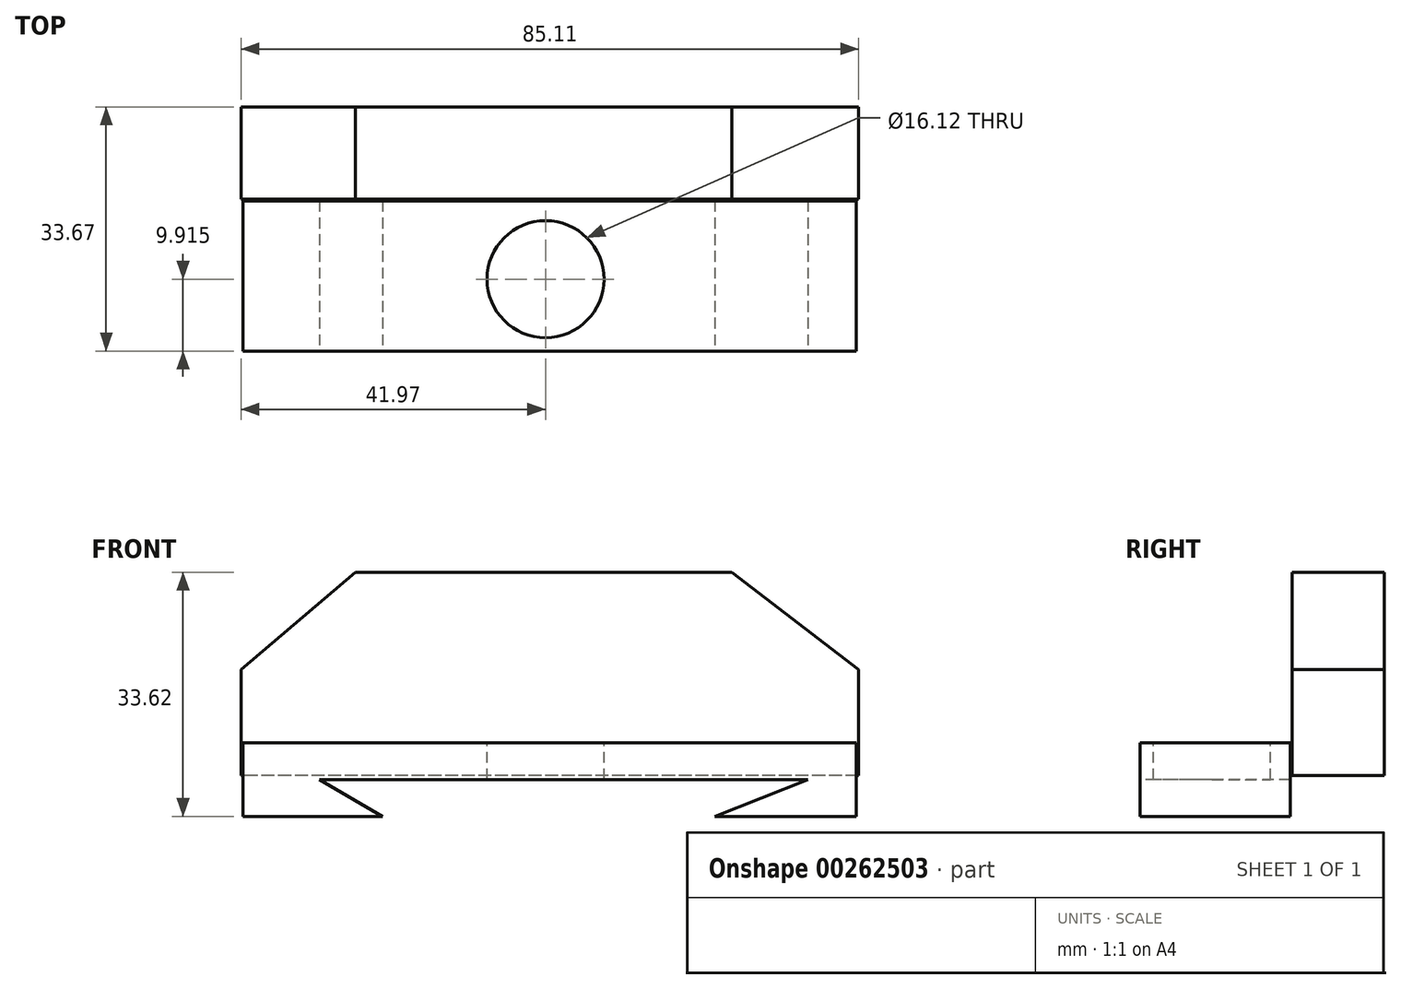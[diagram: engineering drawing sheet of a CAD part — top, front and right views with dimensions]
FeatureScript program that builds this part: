
annotation { "Feature Type Name" : "Feature", "Feature Type Description" : "" }
export const myFeature = defineFeature(function(context is Context, id is Id, definition is map)
    precondition{}
    {
        {
            var Q0;
            Q0=qCreatedBy(makeId("Front.planeOp"),FACE);
            var sketch = newSketch(context, id + "F0", { "sketchPlane" : qUnion([Q0])});
            skLineSegment(sketch, "E0", {"start": v(-26.23, 23.46) * mm, "end": v(25.65, 23.46) * mm});
            skLineSegment(sketch, "E1", {"start": v(25.65, 23.46) * mm, "end": v(43.14, 10.06) * mm});
            skLineSegment(sketch, "E2", {"start": v(43.14, 10.06) * mm, "end": v(25.65, 23.46) * mm});
            skLineSegment(sketch, "E3", {"start": v(-26.23, 23.46) * mm, "end": v(-41.97, 10.06) * mm});
            skLineSegment(sketch, "E4", {"start": v(-41.97, 10.06) * mm, "end": v(-41.97, -4.52) * mm});
            skLineSegment(sketch, "E5", {"start": v(-41.97, -4.52) * mm, "end": v(-41.97, 10.06) * mm});
            skLineSegment(sketch, "E6", {"start": v(43.14, 10.06) * mm, "end": v(43.14, -4.52) * mm});
            skLineSegment(sketch, "E7", {"start": v(43.14, -4.52) * mm, "end": v(-41.97, -4.52) * mm});
            skSolve(sketch);
        }
        {
            var Q0;
            Q0=makeQuery(id+"F0.imprint","IMPRINT",FACE,{"disambiguationData":[TD([[makeQuery(id+"F0.imprint","IMPRINT",EDGE,{"derivedFrom":sQuery(id+"F0.wireOp",EDGE,"E0")}),-1.0]])]});
            extrude(context, id + "F1", {"entities" : qUnion([Q0]), "depth" : 12.7 * mm});
        }
        {
            var Q0;
            Q0=qCreatedBy(makeId("Top.planeOp"),FACE);
            var sketch = newSketch(context, id + "F2", { "sketchPlane" : qUnion([Q0])});
            skLineSegment(sketch, "E8", {"start": v(-41.68, -12.97) * mm, "end": v(-41.68, -33.67) * mm});
            skLineSegment(sketch, "E9", {"start": v(42.85, -12.97) * mm, "end": v(42.85, -33.67) * mm});
            skLineSegment(sketch, "E10", {"start": v(42.85, -33.67) * mm, "end": v(-41.68, -33.67) * mm});
            skLineSegment(sketch, "E11", {"start": v(-41.68, -12.97) * mm, "end": v(42.85, -12.97) * mm});
            skSolve(sketch);
        }
        {
            var Q0;
            Q0=makeQuery(id+"F2.imprint","IMPRINT",FACE,{"disambiguationData":[TD([[makeQuery(id+"F2.imprint","IMPRINT",EDGE,{"derivedFrom":sQuery(id+"F2.wireOp",EDGE,"E8")}),1.0]])]});
            extrude(context, id + "F3", {"entities" : qUnion([Q0]), "oppositeDirection" : true, "depth" : 10.16 * mm});
        }
        {
            var Q0;
            Q0=makeQuery(id+"F3.opExtrude","SWEPT_FACE",FACE,{"disambiguationData":[OSD([sQuery(id+"F2.wireOp",EDGE,"E10")])]});
            var sketch = newSketch(context, id + "F4", { "sketchPlane" : qUnion([Q0])});
            skLineSegment(sketch, "E12", {"start": v(-31.19, -5.08) * mm, "end": v(36.14, -5.08) * mm});
            skPoint(sketch, "E12.startSnap0", {"position": v(-41.68, -5.08) * mm});
            skLineSegment(sketch, "E13", {"start": v(36.14, -5.08) * mm, "end": v(23.32, -10.16) * mm});
            skLineSegment(sketch, "E14", {"start": v(23.32, -10.16) * mm, "end": v(-22.44, -10.16) * mm});
            skLineSegment(sketch, "E15", {"start": v(-22.44, -10.16) * mm, "end": v(-31.19, -5.08) * mm});
            skLineSegment(sketch, "E16", {"start": v(-22.44, -10.16) * mm, "end": v(23.32, -10.16) * mm});
            skSolve(sketch);
        }
        {
            var Q0;
            Q0=makeQuery(id+"F4.imprint","IMPRINT",FACE,{"disambiguationData":[TD([[makeQuery(id+"F4.imprint","IMPRINT",EDGE,{"derivedFrom":sQuery(id+"F4.wireOp",EDGE,"E12")}),-1.0]])]});
            extrude(context, id + "F5", {"entities" : qUnion([Q0]), "operationType" : NewBodyOperationType.REMOVE, "oppositeDirection" : true, "depth" : 76.2 * mm});
        }
        {
            var Q0;
            Q0=makeQuery(id+"F3.opExtrude","CAP_FACE",FACE,{"disambiguationData":[OSD([sQuery(id+"F2.wireOp",EDGE,"E8"),sQuery(id+"F2.wireOp",EDGE,"E9"),sQuery(id+"F2.wireOp",EDGE,"E10"),sQuery(id+"F2.wireOp",EDGE,"E11")])],"isStart":true});
            var sketch = newSketch(context, id + "F6", { "sketchPlane" : qUnion([Q0])});
            skCircle(sketch, "E17", {"center": v(0, -23.76) * mm, "radius": 8.06 * mm});
            skSolve(sketch);
        }
        {
            var Q0;
            Q0=makeQuery(id+"F6.imprint","IMPRINT",FACE,{"disambiguationData":[TD([[makeQuery(id+"F6.imprint","IMPRINT",EDGE,{"derivedFrom":sQuery(id+"F6.wireOp",EDGE,"E17")}),1.0]])]});
            extrude(context, id + "F7", {"entities" : qUnion([Q0]), "operationType" : NewBodyOperationType.REMOVE, "oppositeDirection" : true, "depth" : 25.4 * mm});
        }
    });
